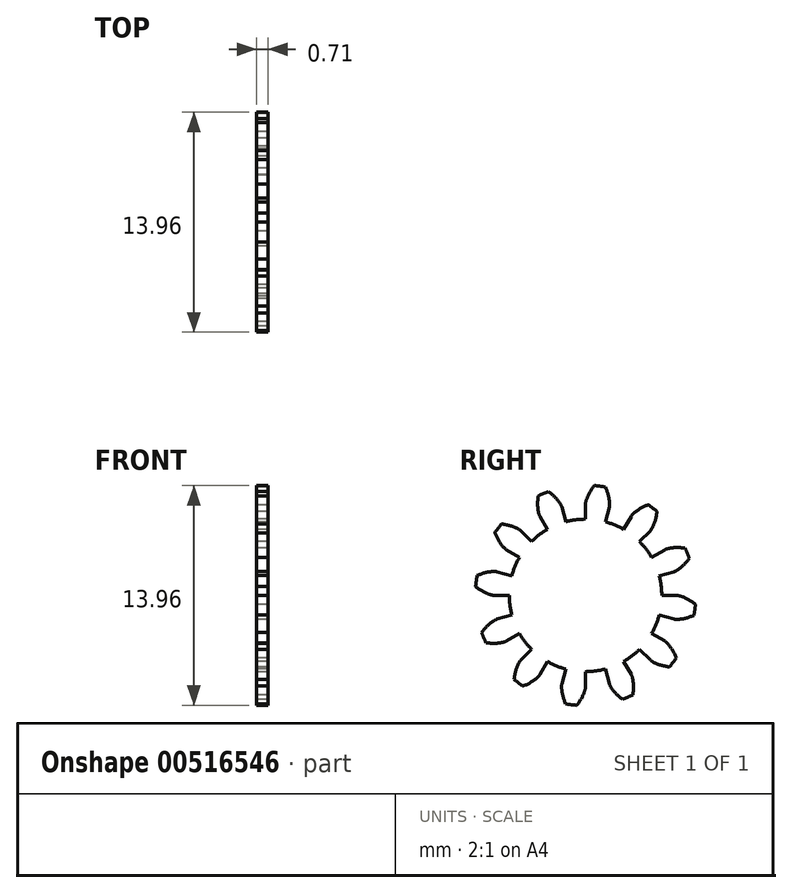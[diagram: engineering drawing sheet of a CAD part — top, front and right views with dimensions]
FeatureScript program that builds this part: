
annotation { "Feature Type Name" : "Feature", "Feature Type Description" : "" }
export const myFeature = defineFeature(function(context is Context, id is Id, definition is map)
    precondition{}
    {
        {
            assignVariable(context, id + "F0", {"name" : "NumberTeeth", "anyValue" : 12});
        }
        {
            assignVariable(context, id + "F1", {"name" : "GearThickness", "anyValue" : 0.7});
        }
        {
            var Q0;
            Q0=qCreatedBy(makeId("Right.planeOp"),FACE);
            var sketch = newSketch(context, id + "F2", { "sketchPlane" : qUnion([Q0])});
            skCircle(sketch, "E0", {"center": v(0, 0) * mm, "radius": 4.84 * mm});
            skCircle(sketch, "E1", {"center": v(0, 0) * mm, "radius": 5.8 * mm, "construction": true});
            skCircle(sketch, "E2", {"center": v(0, 0) * mm, "radius": 6 * mm, "construction": true});
            skCircle(sketch, "E3", {"center": v(0, 0) * mm, "radius": 7 * mm});
            skLineSegment(sketch, "E4", {"start": v(0, 0) * mm, "end": v(-5.8, 0) * mm, "construction": true});
            skLineSegment(sketch, "E5.1.0", {"start": v(0, 0) * mm, "end": v(-5.8, 0.3) * mm, "construction": true});
            skLineSegment(sketch, "E5.2.0", {"start": v(0, 0) * mm, "end": v(-5.78, 0.58) * mm, "construction": true});
            skLineSegment(sketch, "E5.3.0", {"start": v(0, 0) * mm, "end": v(-5.74, 0.87) * mm, "construction": true});
            skLineSegment(sketch, "E5.4.0", {"start": v(0, 0) * mm, "end": v(-5.7, 1.15) * mm, "construction": true});
            skLineSegment(sketch, "E5.5.0", {"start": v(0, 0) * mm, "end": v(-5.63, 1.44) * mm, "construction": true});
            skLineSegment(sketch, "E5.6.0", {"start": v(0, 0) * mm, "end": v(-5.55, 1.72) * mm, "construction": true});
            skLineSegment(sketch, "E5.7.0", {"start": v(0, 0) * mm, "end": v(-5.46, 2) * mm, "construction": true});
            skLineSegment(sketch, "E5.8.0", {"start": v(0, 0) * mm, "end": v(-5.35, 2.26) * mm, "construction": true});
            skLineSegment(sketch, "E5.9.0", {"start": v(0, 0) * mm, "end": v(-5.23, 2.53) * mm, "construction": true});
            skLineSegment(sketch, "E5.10.0", {"start": v(0, 0) * mm, "end": v(-5.1, 2.78) * mm, "construction": true});
            skLineSegment(sketch, "E5.11.0", {"start": v(0, 0) * mm, "end": v(-4.95, 3.04) * mm, "construction": true});
            skLineSegment(sketch, "E5.12.0", {"start": v(0, 0) * mm, "end": v(-4.8, 3.28) * mm, "construction": true});
            skLineSegment(sketch, "E5.13.0", {"start": v(0, 0) * mm, "end": v(-4.62, 3.52) * mm, "construction": true});
            skLineSegment(sketch, "E5.14.0", {"start": v(0, 0) * mm, "end": v(-4.44, 3.74) * mm, "construction": true});
            skLineSegment(sketch, "E5.anchor2", {"start": v(0, 0) * mm, "end": v(-4.44, 3.74) * mm, "construction": true});
            skLineSegment(sketch, "E6", {"start": v(-5.8, 0.3) * mm, "end": v(-5.82, 0) * mm, "construction": true});
            skLineSegment(sketch, "E7", {"start": v(-5.78, 0.58) * mm, "end": v(-5.84, 0) * mm, "construction": true});
            skLineSegment(sketch, "E8", {"start": v(-5.74, 0.87) * mm, "end": v(-5.87, 0) * mm, "construction": true});
            skLineSegment(sketch, "E9", {"start": v(-5.63, 1.44) * mm, "end": v(-5.99, 0.03) * mm, "construction": true});
            skLineSegment(sketch, "E10", {"start": v(-5.55, 1.72) * mm, "end": v(-6.06, 0.05) * mm, "construction": true});
            skLineSegment(sketch, "E11", {"start": v(-5.46, 2) * mm, "end": v(-6.15, 0.08) * mm, "construction": true});
            skLineSegment(sketch, "E12", {"start": v(-5.35, 2.26) * mm, "end": v(-6.26, 0.12) * mm, "construction": true});
            skLineSegment(sketch, "E13", {"start": v(-5.23, 2.53) * mm, "end": v(-6.37, 0.17) * mm, "construction": true});
            skLineSegment(sketch, "E14", {"start": v(-5.1, 2.78) * mm, "end": v(-6.5, 0.24) * mm, "construction": true});
            skLineSegment(sketch, "E15", {"start": v(-4.95, 3.04) * mm, "end": v(-6.62, 0.31) * mm, "construction": true});
            skLineSegment(sketch, "E16", {"start": v(-5.7, 1.15) * mm, "end": v(-5.92, 0.02) * mm, "construction": true});
            skLineSegment(sketch, "E17", {"start": v(-4.8, 3.28) * mm, "end": v(-6.76, 0.4) * mm, "construction": true});
            skLineSegment(sketch, "E18", {"start": v(-4.62, 3.52) * mm, "end": v(-6.9, 0.5) * mm, "construction": true});
            skLineSegment(sketch, "E19", {"start": v(-4.44, 3.74) * mm, "end": v(-7.06, 0.63) * mm, "construction": true});
            skLineSegment(sketch, "E20", {"start": v(0, 0) * mm, "end": v(-5.76, 0.76) * mm, "construction": true});
            skLineSegment(sketch, "E21", {"start": v(-4.84, 0) * mm, "end": v(-5.8, 0) * mm});
            skLineSegment(sketch, "E22.MirrorCS", {"start": v(-4.68, 1.25) * mm, "end": v(-5.61, 1.5) * mm});
            skFitSpline(sketch, "E23", {"points": [v(-5.8, 0) * mm, v(-5.82, 0) * mm, v(-5.84, 0) * mm, v(-5.87, 0) * mm, v(-5.92, 0.02) * mm, v(-5.99, 0.03) * mm, v(-6.06, 0.05) * mm, v(-6.15, 0.08) * mm, v(-6.26, 0.12) * mm, v(-6.37, 0.17) * mm, v(-6.5, 0.24) * mm, v(-6.62, 0.31) * mm, v(-6.76, 0.4) * mm, v(-6.9, 0.5) * mm, v(-7.06, 0.63) * mm], "startDerivative": vector(-0.88, 0) * mm, "endDerivative": vector(-0.94, 0.8) * mm});
            skLineSegment(sketch, "E24", {"start": v(-7.06, 0.63) * mm, "end": v(-14.73, 7.09) * mm, "construction": true});
            skFitSpline(sketch, "E25.MirrorCS", {"points": [v(-5.61, 1.5) * mm, v(-5.62, 1.5) * mm, v(-5.64, 1.5) * mm, v(-5.68, 1.51) * mm, v(-5.73, 1.52) * mm, v(-5.8, 1.52) * mm, v(-5.87, 1.52) * mm, v(-5.97, 1.51) * mm, v(-6.07, 1.5) * mm, v(-6.2, 1.48) * mm, v(-6.33, 1.45) * mm, v(-6.48, 1.41) * mm, v(-6.64, 1.36) * mm, v(-6.8, 1.3) * mm, v(-6.99, 1.22) * mm], "startDerivative": vector(-0.85, 0.23) * mm, "endDerivative": vector(-1.12, -0.52) * mm});
            skSolve(sketch);
        }
        {
            var Q0;
            {var subQ0=sQuery(id+"F2.wireOp",EDGE,"E0");var subQ27=makeQuery(id+"F2.imprint","INTERSECT",VERTEX,{"derivedFrom":[subQ0,sQuery(id+"F2.wireOp",EDGE,"10ea1024-8cf5-41f5-a75f-a634b86921f3.10.0")]});Q0=makeQuery(id+"F2.imprint","IMPRINT",FACE,{"disambiguationData":[TD([[makeQuery(id+"F2.imprint","IMPRINT",EDGE,{"disambiguationData":[TD([[subQ27,-1.0]])],"derivedFrom":subQ0}),1.0]])]});}
            var Q1;
            {var subQ0=sQuery(id+"F2.wireOp",EDGE,"10ea1024-8cf5-41f5-a75f-a634b86921f3.1.0");Q1=makeQuery(id+"F2.imprint","IMPRINT",FACE,{"disambiguationData":[TD([[makeQuery(id+"F2.imprint","IMPRINT",EDGE,{"derivedFrom":subQ0}),-1.0]])]});}
            var Q2;
            {var subQ7=sQuery(id+"F2.wireOp",EDGE,"10ea1024-8cf5-41f5-a75f-a634b86921f3.2.0");Q2=makeQuery(id+"F2.imprint","IMPRINT",FACE,{"disambiguationData":[TD([[makeQuery(id+"F2.imprint","IMPRINT",EDGE,{"derivedFrom":subQ7}),-1.0]])]});}
            var Q3;
            {var subQ8=sQuery(id+"F2.wireOp",EDGE,"10ea1024-8cf5-41f5-a75f-a634b86921f3.3.0");Q3=makeQuery(id+"F2.imprint","IMPRINT",FACE,{"disambiguationData":[TD([[makeQuery(id+"F2.imprint","IMPRINT",EDGE,{"derivedFrom":subQ8}),-1.0]])]});}
            var Q4;
            {var subQ2=sQuery(id+"F2.wireOp",EDGE,"10ea1024-8cf5-41f5-a75f-a634b86921f3.4.0");Q4=makeQuery(id+"F2.imprint","IMPRINT",FACE,{"disambiguationData":[TD([[makeQuery(id+"F2.imprint","IMPRINT",EDGE,{"derivedFrom":subQ2}),-1.0]])]});}
            var Q5;
            {var subQ8=sQuery(id+"F2.wireOp",EDGE,"10ea1024-8cf5-41f5-a75f-a634b86921f3.5.0");Q5=makeQuery(id+"F2.imprint","IMPRINT",FACE,{"disambiguationData":[TD([[makeQuery(id+"F2.imprint","IMPRINT",EDGE,{"derivedFrom":subQ8}),-1.0]])]});}
            var Q6;
            {var subQ3=sQuery(id+"F2.wireOp",EDGE,"10ea1024-8cf5-41f5-a75f-a634b86921f3.6.0");Q6=makeQuery(id+"F2.imprint","IMPRINT",FACE,{"disambiguationData":[TD([[makeQuery(id+"F2.imprint","IMPRINT",EDGE,{"derivedFrom":subQ3}),-1.0]])]});}
            var Q7;
            {var subQ0=sQuery(id+"F2.wireOp",EDGE,"10ea1024-8cf5-41f5-a75f-a634b86921f3.7.0");Q7=makeQuery(id+"F2.imprint","IMPRINT",FACE,{"disambiguationData":[TD([[makeQuery(id+"F2.imprint","IMPRINT",EDGE,{"derivedFrom":subQ0}),-1.0]])]});}
            var Q8;
            {var subQ5=sQuery(id+"F2.wireOp",EDGE,"10ea1024-8cf5-41f5-a75f-a634b86921f3.8.0");Q8=makeQuery(id+"F2.imprint","IMPRINT",FACE,{"disambiguationData":[TD([[makeQuery(id+"F2.imprint","IMPRINT",EDGE,{"derivedFrom":subQ5}),-1.0]])]});}
            var Q9;
            {var subQ1=sQuery(id+"F2.wireOp",EDGE,"10ea1024-8cf5-41f5-a75f-a634b86921f3.9.0");Q9=makeQuery(id+"F2.imprint","IMPRINT",FACE,{"disambiguationData":[TD([[makeQuery(id+"F2.imprint","IMPRINT",EDGE,{"derivedFrom":subQ1}),-1.0]])]});}
            var Q10;
            {var subQ5=sQuery(id+"F2.wireOp",EDGE,"10ea1024-8cf5-41f5-a75f-a634b86921f3.10.0");Q10=makeQuery(id+"F2.imprint","IMPRINT",FACE,{"disambiguationData":[TD([[makeQuery(id+"F2.imprint","IMPRINT",EDGE,{"derivedFrom":subQ5}),-1.0]])]});}
            var Q11;
            {var subQ8=sQuery(id+"F2.wireOp",EDGE,"10ea1024-8cf5-41f5-a75f-a634b86921f3.11.0");Q11=makeQuery(id+"F2.imprint","IMPRINT",FACE,{"disambiguationData":[TD([[makeQuery(id+"F2.imprint","IMPRINT",EDGE,{"derivedFrom":subQ8}),-1.0]])]});}
            var Q12;
            {var subQ2=sQuery(id+"F2.wireOp",EDGE,"10ea1024-8cf5-41f5-a75f-a634b86921f3.12.0");Q12=makeQuery(id+"F2.imprint","IMPRINT",FACE,{"disambiguationData":[TD([[makeQuery(id+"F2.imprint","IMPRINT",EDGE,{"derivedFrom":subQ2}),-1.0]])]});}
            var Q13;
            {var subQ3=sQuery(id+"F2.wireOp",EDGE,"10ea1024-8cf5-41f5-a75f-a634b86921f3.13.0");Q13=makeQuery(id+"F2.imprint","IMPRINT",FACE,{"disambiguationData":[TD([[makeQuery(id+"F2.imprint","IMPRINT",EDGE,{"derivedFrom":subQ3}),-1.0]])]});}
            var Q14;
            {var subQ0=sQuery(id+"F2.wireOp",EDGE,"10ea1024-8cf5-41f5-a75f-a634b86921f3.14.0");Q14=makeQuery(id+"F2.imprint","IMPRINT",FACE,{"disambiguationData":[TD([[makeQuery(id+"F2.imprint","IMPRINT",EDGE,{"derivedFrom":subQ0}),-1.0]])]});}
            var Q15;
            {var subQ6=sQuery(id+"F2.wireOp",EDGE,"10ea1024-8cf5-41f5-a75f-a634b86921f3.15.0");Q15=makeQuery(id+"F2.imprint","IMPRINT",FACE,{"disambiguationData":[TD([[makeQuery(id+"F2.imprint","IMPRINT",EDGE,{"derivedFrom":subQ6}),-1.0]])]});}
            var Q16;
            {var subQ5=sQuery(id+"F2.wireOp",EDGE,"10ea1024-8cf5-41f5-a75f-a634b86921f3.16.0");Q16=makeQuery(id+"F2.imprint","IMPRINT",FACE,{"disambiguationData":[TD([[makeQuery(id+"F2.imprint","IMPRINT",EDGE,{"derivedFrom":subQ5}),-1.0]])]});}
            var Q17;
            {var subQ7=sQuery(id+"F2.wireOp",EDGE,"10ea1024-8cf5-41f5-a75f-a634b86921f3.17.0");Q17=makeQuery(id+"F2.imprint","IMPRINT",FACE,{"disambiguationData":[TD([[makeQuery(id+"F2.imprint","IMPRINT",EDGE,{"derivedFrom":subQ7}),-1.0]])]});}
            var Q18;
            {var subQ5=sQuery(id+"F2.wireOp",EDGE,"10ea1024-8cf5-41f5-a75f-a634b86921f3.18.0");Q18=makeQuery(id+"F2.imprint","IMPRINT",FACE,{"disambiguationData":[TD([[makeQuery(id+"F2.imprint","IMPRINT",EDGE,{"derivedFrom":subQ5}),-1.0]])]});}
            var Q19;
            {var subQ8=sQuery(id+"F2.wireOp",EDGE,"10ea1024-8cf5-41f5-a75f-a634b86921f3.19.0");Q19=makeQuery(id+"F2.imprint","IMPRINT",FACE,{"disambiguationData":[TD([[makeQuery(id+"F2.imprint","IMPRINT",EDGE,{"derivedFrom":subQ8}),-1.0]])]});}
            var Q20;
            {var subQ8=sQuery(id+"F2.wireOp",EDGE,"E21");Q20=makeQuery(id+"F2.imprint","IMPRINT",FACE,{"disambiguationData":[TD([[makeQuery(id+"F2.imprint","IMPRINT",EDGE,{"derivedFrom":subQ8}),-1.0]])]});}
            extrude(context, id + "F3", {"entities" : qUnion([Q0, Q1, Q2, Q3, Q4, Q5, Q6, Q7, Q8, Q9, Q10, Q11, Q12, Q13, Q14, Q15, Q16, Q17, Q18, Q19, Q20]), "depth" : (getVariable(context, 'GearThickness')) * mm, "offsetDistance" : 25 * mm});
        }
        {
            var Q0;
            Q0=makeQuery(id+"F3.opExtrude","SWEPT_FACE",FACE,{"disambiguationData":[OSD([sQuery(id+"F2.wireOp",EDGE,"E25.MirrorCS")])]});
            var Q1;
            Q1=makeQuery(id+"F3.opExtrude","SWEPT_FACE",FACE,{"disambiguationData":[OSD([sQuery(id+"F2.wireOp",EDGE,"E23")])]});
            var Q2;
            Q2=makeQuery(id+"F3.opExtrude","SWEPT_FACE",FACE,{"disambiguationData":[OSD([sQuery(id+"F2.wireOp",EDGE,"E3")])]});
            var Q3;
            Q3=makeQuery(id+"F3.opExtrude","SWEPT_FACE",FACE,{"disambiguationData":[OSD([sQuery(id+"F2.wireOp",EDGE,"E22.MirrorCS")])]});
            var Q4;
            Q4=makeQuery(id+"F3.opExtrude","SWEPT_FACE",FACE,{"disambiguationData":[OSD([sQuery(id+"F2.wireOp",EDGE,"E21")])]});
            var Q5;
            Q5=makeQuery(id+"F3.opExtrude","SWEPT_FACE",FACE,{"disambiguationData":[OSD([sQuery(id+"F2.wireOp",EDGE,"E0")])]});
            circularPattern(context, id + "F4", {"faces" : qUnion([Q0, Q1, Q2, Q3, Q4]), "axis" : qUnion([Q5]), "angle" : 360 * degree, "instanceCount" : getVariable(context, 'NumberTeeth'), "equalSpace" : true, "patternType" : PatternType.FACE});
        }
    });
